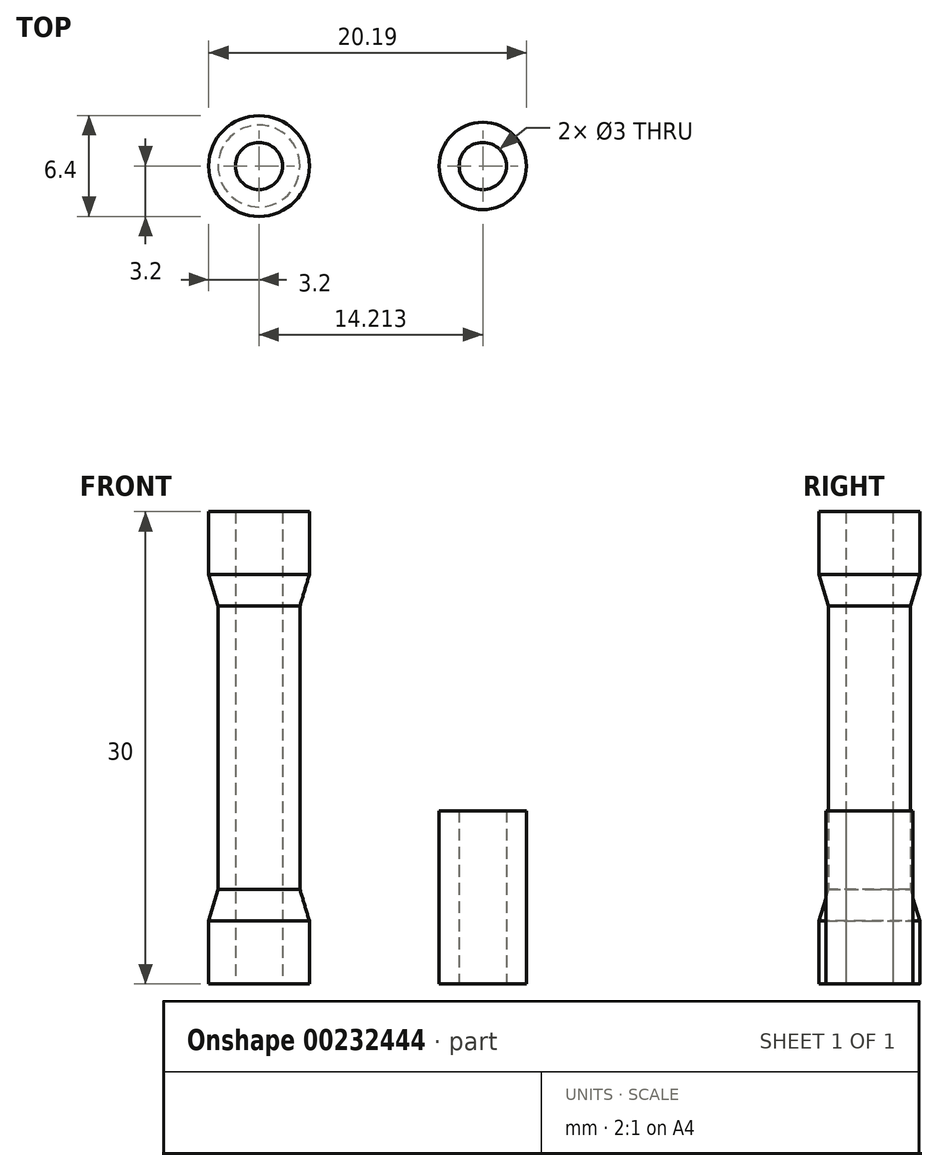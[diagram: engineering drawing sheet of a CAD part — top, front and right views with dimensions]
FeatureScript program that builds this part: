
annotation { "Feature Type Name" : "Feature", "Feature Type Description" : "" }
export const myFeature = defineFeature(function(context is Context, id is Id, definition is map)
    precondition{}
    {
        {
            var Q0;
            Q0=qCreatedBy(makeId("Top.planeOp"),FACE);
            var sketch = newSketch(context, id + "F0", { "sketchPlane" : qUnion([Q0])});
            skCircle(sketch, "E0", {"center": v(0, 0) * mm, "radius": 3.2 * mm});
            skSolve(sketch);
        }
        {
            var Q0;
            Q0=qSketchRegion(id+"F0",true);
            extrude(context, id + "F1", {"entities" : qUnion([Q0]), "depth" : 4 * mm});
        }
        {
            var Q0;
            Q0=qCreatedBy(makeId("Top.planeOp"),FACE);
            cPlane(context, id + "F2", {"entities" : qUnion([Q0]), "cplaneType" : CPlaneType.OFFSET, "offset" : 6 * mm, "width" : 150 * mm, "height" : 150 * mm});
        }
        {
            var Q0;
            Q0=qCreatedBy(id+"F2.planeOp",FACE);
            var sketch = newSketch(context, id + "F3", { "sketchPlane" : qUnion([Q0])});
            skCircle(sketch, "E1", {"center": v(0, 0) * mm, "radius": 2.6 * mm});
            skSolve(sketch);
        }
        {
            var Q1;
            Q1=makeQuery(id+"F1.opExtrude","CAP_FACE",FACE,{"disambiguationData":[OSD([sQuery(id+"F0.wireOp",EDGE,"E0")])],"isStart":false});
            var Q2;
            Q2=makeQuery(id+"F3.imprint","IMPRINT",FACE,{"disambiguationData":[TD([[makeQuery(id+"F3.imprint","IMPRINT",EDGE,{"derivedFrom":sQuery(id+"F3.wireOp",EDGE,"E1")}),1.0]])]});
            loft(context, id + "F4", {"operationType" : NewBodyOperationType.ADD, "sheetProfilesArray" : [{ "sheetProfileEntities" : qUnion([Q1]) }, { "sheetProfileEntities" : qUnion([Q2]) }]});
        }
        {
            var Q0;
            Q0=qCreatedBy(id+"F2.planeOp",FACE);
            cPlane(context, id + "F5", {"entities" : qUnion([Q0]), "cplaneType" : CPlaneType.OFFSET, "offset" : 18 * mm, "width" : 150 * mm, "height" : 150 * mm});
        }
        {
            var Q0;
            Q0=qCreatedBy(id+"F5.planeOp",FACE);
            var sketch = newSketch(context, id + "F6", { "sketchPlane" : qUnion([Q0])});
            skCircle(sketch, "E2", {"center": v(0, 0) * mm, "radius": 2.6 * mm});
            skSolve(sketch);
        }
        {
            var Q0;
            Q0=qCreatedBy(id+"F5.planeOp",FACE);
            cPlane(context, id + "F7", {"entities" : qUnion([Q0]), "cplaneType" : CPlaneType.OFFSET, "offset" : 2 * mm, "width" : 150 * mm, "height" : 150 * mm});
        }
        {
            var Q0;
            Q0=qCreatedBy(id+"F7.planeOp",FACE);
            var sketch = newSketch(context, id + "F8", { "sketchPlane" : qUnion([Q0])});
            skCircle(sketch, "E3", {"center": v(0, 0) * mm, "radius": 3.2 * mm});
            skSolve(sketch);
        }
        {
            var Q0;
            Q0=qSketchRegion(id+"F3",true);
            extrude(context, id + "F9", {"entities" : qUnion([Q0]), "operationType" : NewBodyOperationType.ADD, "depth" : 18 * mm});
        }
        {
            var Q1;
            Q1=makeQuery(id+"F6.imprint","IMPRINT",FACE,{"disambiguationData":[TD([[makeQuery(id+"F6.imprint","IMPRINT",EDGE,{"derivedFrom":sQuery(id+"F6.wireOp",EDGE,"E2")}),1.0]])]});
            var Q2;
            Q2=makeQuery(id+"F8.imprint","IMPRINT",FACE,{"disambiguationData":[TD([[makeQuery(id+"F8.imprint","IMPRINT",EDGE,{"derivedFrom":sQuery(id+"F8.wireOp",EDGE,"E3")}),1.0]])]});
            loft(context, id + "F10", {"operationType" : NewBodyOperationType.ADD, "sheetProfilesArray" : [{ "sheetProfileEntities" : qUnion([Q1]) }, { "sheetProfileEntities" : qUnion([Q2]) }]});
        }
        {
            var Q0;
            Q0=qSketchRegion(id+"F8",true);
            extrude(context, id + "F11", {"entities" : qUnion([Q0]), "operationType" : NewBodyOperationType.ADD, "depth" : 4 * mm});
        }
        {
            var Q0;
            Q0=qCreatedBy(makeId("Top.planeOp"),FACE);
            var sketch = newSketch(context, id + "F12", { "sketchPlane" : qUnion([Q0])});
            skCircle(sketch, "E4", {"center": v(0, 0) * mm, "radius": 1.5 * mm});
            skSolve(sketch);
        }
        {
            var Q0;
            Q0=qSketchRegion(id+"F12",true);
            extrude(context, id + "F13", {"entities" : qUnion([Q0]), "operationType" : NewBodyOperationType.REMOVE, "depth" : 50 * mm});
        }
        {
            var Q0;
            Q0=qCreatedBy(makeId("Top.planeOp"),FACE);
            var sketch = newSketch(context, id + "F14", { "sketchPlane" : qUnion([Q0])});
            skCircle(sketch, "E5", {"center": v(14.21, 0) * mm, "radius": 2.77 * mm});
            skCircle(sketch, "E6", {"center": v(14.21, 0) * mm, "radius": 1.5 * mm});
            skSolve(sketch);
        }
        {
            var Q0;
            Q0=qSketchRegion(id+"F14",true);
            extrude(context, id + "F15", {"entities" : qUnion([Q0]), "depth" : 11 * mm});
        }
    });
